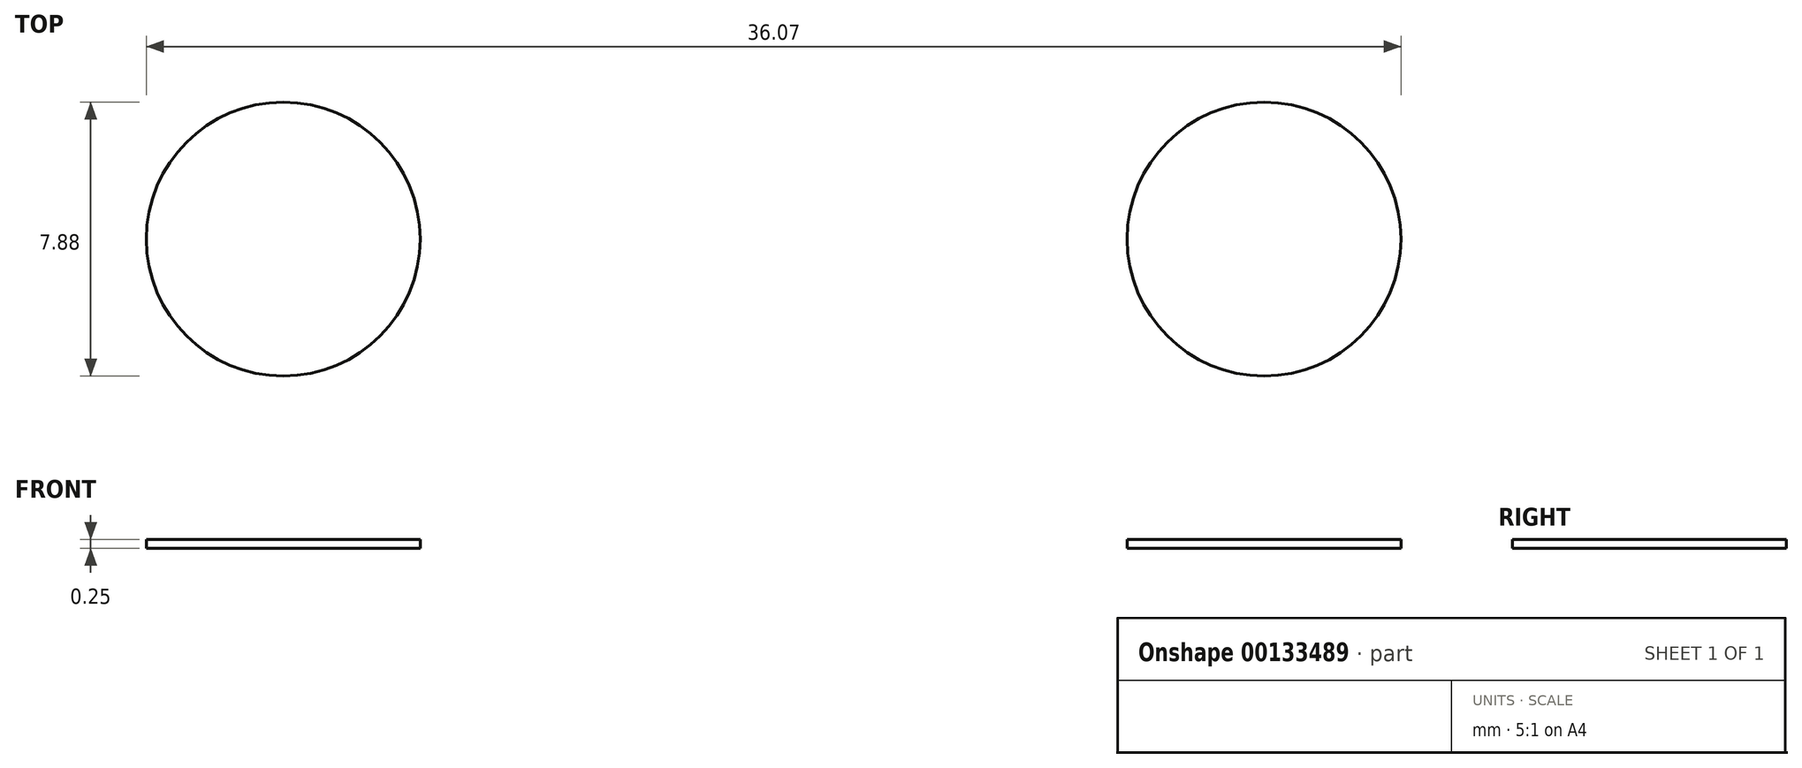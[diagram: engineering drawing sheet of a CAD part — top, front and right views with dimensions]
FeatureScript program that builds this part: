
annotation { "Feature Type Name" : "Feature", "Feature Type Description" : "" }
export const myFeature = defineFeature(function(context is Context, id is Id, definition is map)
    precondition{}
    {
        {
            var Q0;
            Q0=qCreatedBy(makeId("Top.planeOp"),FACE);
            var sketch = newSketch(context, id + "F0", { "sketchPlane" : qUnion([Q0])});
            skCircle(sketch, "E0", {"center": v(-14.61, 0) * mm, "radius": 3.94 * mm});
            skCircle(sketch, "E1", {"center": v(13.58, 0) * mm, "radius": 3.94 * mm});
            skSolve(sketch);
        }
        {
            var Q0;
            Q0 = qSketchRegion(id + "F0", true);
            extrude(context, id + "F1", {"entities" : qUnion([Q0]), "depth" : 0.25 * mm});
        }
        {
            var Q0;
            Q0=qCreatedBy(makeId("Front.planeOp"),FACE);
            var sketch = newSketch(context, id + "F2", { "sketchPlane" : qUnion([Q0])});
            skArc(sketch, "E2", {"start": v(-10.69, 0) * mm, "mid": v(-0.55, -7.5) * mm, "end": v(9.58, 0) * mm});
            skSolve(sketch);
        }
        {
            var Q0;
            Q0=sQuery(id+"F2.wireOp",EDGE,"E2");
            extrude(context, id + "F3", {"bodyType" : ToolBodyType.SURFACE, "surfaceEntities" : qUnion([Q0]), "endBound" : BoundingType.SYMMETRIC, "depth" : 7.62 * mm});
        }
    });
